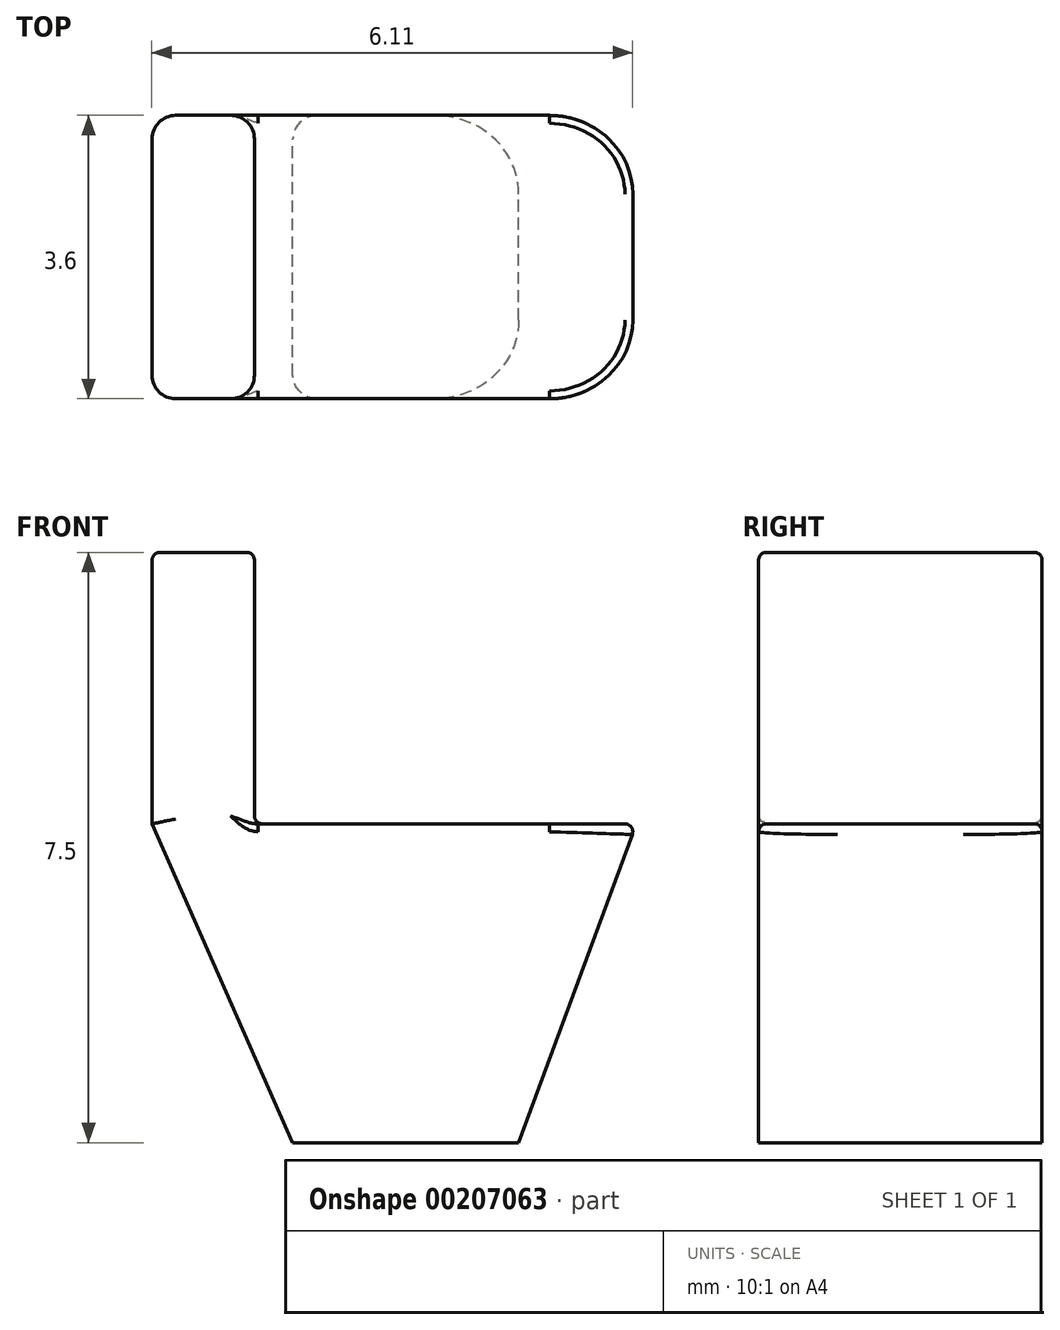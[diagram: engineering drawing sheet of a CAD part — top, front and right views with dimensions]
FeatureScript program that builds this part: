
annotation { "Feature Type Name" : "Feature", "Feature Type Description" : "" }
export const myFeature = defineFeature(function(context is Context, id is Id, definition is map)
    precondition{}
    {
        {
            var Q0;
            Q0=qCreatedBy(makeId("Front.planeOp"),FACE);
            var sketch = newSketch(context, id + "F0", { "sketchPlane" : qUnion([Q0])});
            skLineSegment(sketch, "E0", {"start": v(1.58, 0) * mm, "end": v(3.07, 4.05) * mm});
            skLineSegment(sketch, "E1", {"start": v(3.07, 4.05) * mm, "end": v(-3.08, 4.05) * mm});
            skLineSegment(sketch, "E2", {"start": v(-3.08, 4.05) * mm, "end": v(-1.29, 0) * mm});
            skLineSegment(sketch, "E3", {"start": v(-1.29, 0) * mm, "end": v(1.58, 0) * mm});
            skLineSegment(sketch, "E4", {"start": v(-3.08, 4.05) * mm, "end": v(-3.08, 7.5) * mm});
            skLineSegment(sketch, "E5", {"start": v(-3.08, 7.5) * mm, "end": v(-1.78, 7.5) * mm});
            skLineSegment(sketch, "E6", {"start": v(-1.78, 7.5) * mm, "end": v(-1.78, 4.05) * mm});
            skSolve(sketch);
        }
        {
            var Q0;
            Q0=makeQuery(id+"F0.imprint","IMPRINT",FACE,{"disambiguationData":[TD([[makeQuery(id+"F0.imprint","IMPRINT",EDGE,{"derivedFrom":sQuery(id+"F0.wireOp",EDGE,"E0")}),1.0]])]});
            var Q1;
            {var subQ0=sQuery(id+"F0.wireOp",EDGE,"E4");Q1=makeQuery(id+"F0.imprint","IMPRINT",FACE,{"disambiguationData":[TD([[makeQuery(id+"F0.imprint","IMPRINT",EDGE,{"derivedFrom":subQ0}),-1.0]])]});}
            extrude(context, id + "F1", {"entities" : qUnion([Q0, Q1]), "depth" : 1.8 * mm, "offsetDistance" : 25 * mm});
        }
        {
            var Q0;
            Q0=makeQuery(id+"F1.opExtrude","CAP_EDGE",EDGE,{"disambiguationData":[OSD([sQuery(id+"F0.wireOp",EDGE,"E0")])],"isStart":true});
            fillet(context, id + "F2", {"entities" : qUnion([Q0]), "tangentPropagation" : true, "radius" : 1 * mm, "defaultsChanged" : true, "vertexSettings" : [], "allowEdgeOverflow" : false});
        }
        {
            var Q0;
            Q0=makeQuery(id+"F1.opExtrude","CAP_EDGE",EDGE,{"disambiguationData":[OSD([sQuery(id+"F0.wireOp",EDGE,"E6")])],"isStart":true});
            var Q1;
            Q1=makeQuery(id+"F1.opExtrude","CAP_EDGE",EDGE,{"disambiguationData":[OSD([sQuery(id+"F0.wireOp",EDGE,"E4")])],"isStart":true});
            var Q2;
            Q2=makeQuery(id+"F1.opExtrude","CAP_EDGE",EDGE,{"disambiguationData":[OSD([sQuery(id+"F0.wireOp",EDGE,"E2")])],"isStart":true});
            fillet(context, id + "F3", {"entities" : qUnion([Q0, Q1, Q2]), "tangentPropagation" : true, "radius" : 0.3 * mm, "defaultsChanged" : false, "vertexSettings" : [], "allowEdgeOverflow" : false});
        }
        {
            var Q0;
            Q0=makeQuery(id+"F1.opExtrude","CAP_EDGE",EDGE,{"disambiguationData":[OSD([sQuery(id+"F0.wireOp",EDGE,"E1")])],"isStart":true});
            var Q1;
            Q1=makeQuery(id+"F2.opFillet","BLEND_EDGE",EDGE,{"blendedFrom":[makeQuery(id+"F1.opExtrude","CAP_EDGE",EDGE,{"disambiguationData":[OSD([sQuery(id+"F0.wireOp",EDGE,"E0")])],"isStart":true}),makeQuery(id+"F1.opExtrude","SWEPT_FACE",FACE,{"disambiguationData":[OSD([sQuery(id+"F0.wireOp",EDGE,"E1")])]})],"blendedInto":[makeQuery(id+"F1.opExtrude","SWEPT_FACE",FACE,{"disambiguationData":[OSD([sQuery(id+"F0.wireOp",EDGE,"E1")])]})]});
            var Q2;
            Q2=makeQuery(id+"F1.opExtrude","SWEPT_EDGE",EDGE,{"disambiguationData":[OSD([sQuery(id+"F0.wireOp",EDGE,"E1"),sQuery(id+"F0.wireOp",EDGE,"E6")])]});
            var Q3;
            Q3=makeQuery(id+"F1.opExtrude","SWEPT_EDGE",EDGE,{"disambiguationData":[OSD([sQuery(id+"F0.wireOp",EDGE,"E5"),sQuery(id+"F0.wireOp",EDGE,"E6")])]});
            fillet(context, id + "F4", {"entities" : qUnion([Q0, Q1, Q2, Q3]), "tangentPropagation" : true, "radius" : 0.1 * mm, "defaultsChanged" : false, "vertexSettings" : [], "allowEdgeOverflow" : false});
        }
        {
            var Q0;
            Q0=makeQuery(id+"F1.opExtrude","SWEPT_BODY",BODY,{"disambiguationData":[OSD([sQuery(id+"F0.wireOp",EDGE,"E0"),sQuery(id+"F0.wireOp",EDGE,"E1"),sQuery(id+"F0.wireOp",EDGE,"E2"),sQuery(id+"F0.wireOp",EDGE,"E3"),sQuery(id+"F0.wireOp",EDGE,"UsB9QK7p-PDoR-j2On-BkPt-gVeZGXv6EjAN"),sQuery(id+"F0.wireOp",EDGE,"mMyykxZ5-Uwu0-4WvI-wPpX-SZhDqpEvVsrC"),sQuery(id+"F0.wireOp",EDGE,"RR3ntv1R-G0sh-bIKL-7vHR-9fO5geb81D5f"),sQuery(id+"F0.wireOp",EDGE,"ZuhlJylm-KI3R-8HLj-80bb-YD9U6Zjf2qiN"),sQuery(id+"F0.wireOp",EDGE,"qtU0MKkZ-S1hf-6OBB-Y10r-008iphQahwGy"),sQuery(id+"F0.wireOp",EDGE,"Lv2M0ICj-3I2J-HVah-3oS6-CJDq6w3jNvl3"),sQuery(id+"F0.wireOp",EDGE,"E4"),sQuery(id+"F0.wireOp",EDGE,"E5"),sQuery(id+"F0.wireOp",EDGE,"E6")])]});
            var Q1;
            Q1=makeQuery(id+"F1.opExtrude","CAP_FACE",FACE,{"disambiguationData":[OSD([sQuery(id+"F0.wireOp",EDGE,"E0"),sQuery(id+"F0.wireOp",EDGE,"E1"),sQuery(id+"F0.wireOp",EDGE,"E2"),sQuery(id+"F0.wireOp",EDGE,"E3"),sQuery(id+"F0.wireOp",EDGE,"UsB9QK7p-PDoR-j2On-BkPt-gVeZGXv6EjAN"),sQuery(id+"F0.wireOp",EDGE,"mMyykxZ5-Uwu0-4WvI-wPpX-SZhDqpEvVsrC"),sQuery(id+"F0.wireOp",EDGE,"RR3ntv1R-G0sh-bIKL-7vHR-9fO5geb81D5f"),sQuery(id+"F0.wireOp",EDGE,"ZuhlJylm-KI3R-8HLj-80bb-YD9U6Zjf2qiN"),sQuery(id+"F0.wireOp",EDGE,"qtU0MKkZ-S1hf-6OBB-Y10r-008iphQahwGy"),sQuery(id+"F0.wireOp",EDGE,"Lv2M0ICj-3I2J-HVah-3oS6-CJDq6w3jNvl3"),sQuery(id+"F0.wireOp",EDGE,"E4"),sQuery(id+"F0.wireOp",EDGE,"E5"),sQuery(id+"F0.wireOp",EDGE,"E6")])],"isStart":false});
            mirror(context, id + "F5", {"operationType" : NewBodyOperationType.ADD, "entities" : qUnion([Q0]), "mirrorPlane" : qUnion([Q1])});
        }
    });
